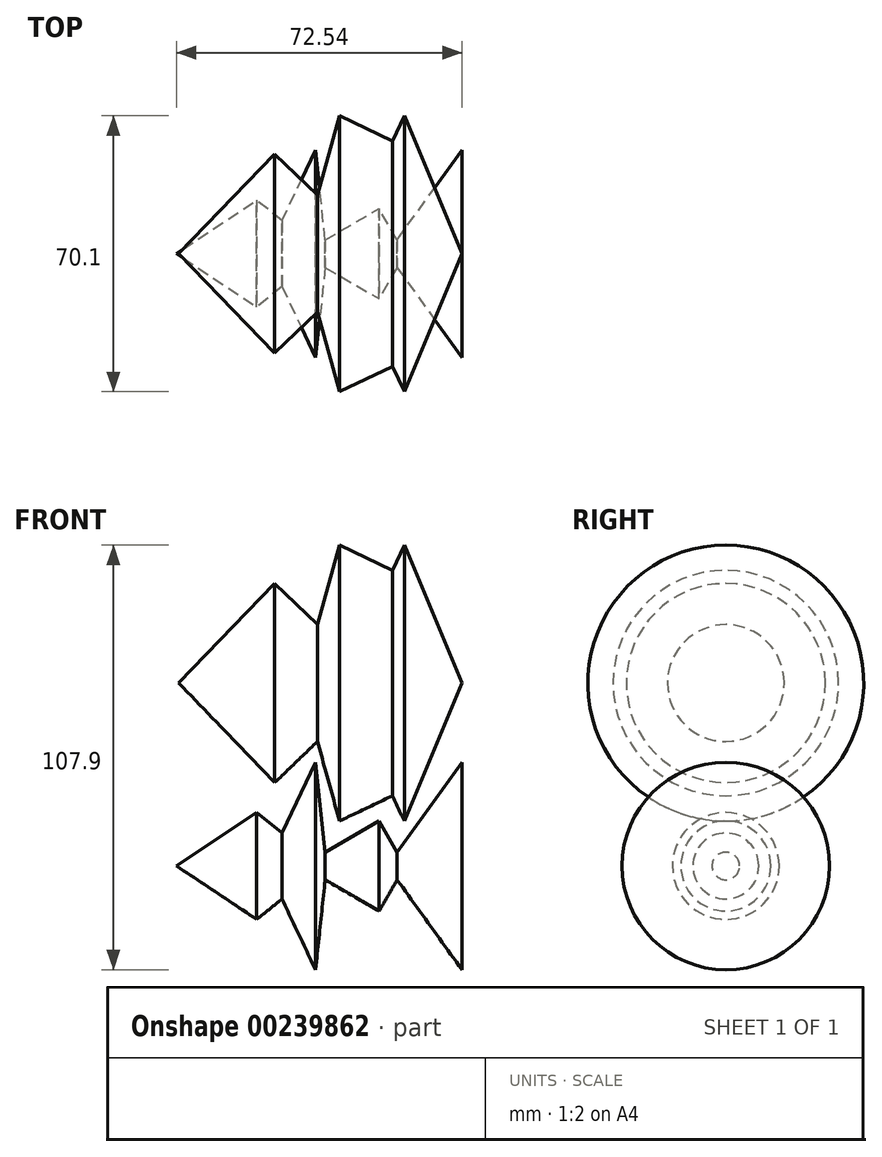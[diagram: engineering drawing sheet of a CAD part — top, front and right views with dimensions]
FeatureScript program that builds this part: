
annotation { "Feature Type Name" : "Feature", "Feature Type Description" : "" }
export const myFeature = defineFeature(function(context is Context, id is Id, definition is map)
    precondition{}
    {
        {
            var Q0;
            Q0=qCreatedBy(makeId("Front.planeOp"),FACE);
            var sketch = newSketch(context, id + "F0", { "sketchPlane" : qUnion([Q0])});
            skLineSegment(sketch, "E0", {"start": v(0, 0) * mm, "end": v(-72.54, 0) * mm});
            skLineSegment(sketch, "E1", {"start": v(-72.54, 0) * mm, "end": v(-52.12, 13.56) * mm});
            skLineSegment(sketch, "E2", {"start": v(-52.12, 13.56) * mm, "end": v(-45.72, 8.38) * mm});
            skLineSegment(sketch, "E3", {"start": v(-45.72, 8.38) * mm, "end": v(-37.19, 26.37) * mm});
            skLineSegment(sketch, "E4", {"start": v(-37.19, 26.37) * mm, "end": v(-34.75, 3.5) * mm});
            skLineSegment(sketch, "E5", {"start": v(-34.75, 3.5) * mm, "end": v(-21.03, 11.43) * mm});
            skLineSegment(sketch, "E6", {"start": v(-21.03, 11.43) * mm, "end": v(-16.45, 3.5) * mm});
            skLineSegment(sketch, "E7", {"start": v(-16.45, 3.5) * mm, "end": v(0, 26.37) * mm});
            skLineSegment(sketch, "E8", {"start": v(0, 26.37) * mm, "end": v(0, 0) * mm});
            skSolve(sketch);
        }
        {
            var Q0;
            Q0=qCreatedBy(makeId("Front.planeOp"),FACE);
            var sketch = newSketch(context, id + "F1", { "sketchPlane" : qUnion([Q0])});
            skLineSegment(sketch, "E9", {"start": v(0, 46.48) * mm, "end": v(-71.93, 46.48) * mm});
            skLineSegment(sketch, "E10", {"start": v(-71.93, 46.48) * mm, "end": v(-47.55, 21.18) * mm});
            skLineSegment(sketch, "E11", {"start": v(-47.55, 21.18) * mm, "end": v(-36.7, 31.64) * mm});
            skLineSegment(sketch, "E12", {"start": v(-36.7, 31.64) * mm, "end": v(-31.09, 11.43) * mm});
            skLineSegment(sketch, "E13", {"start": v(-31.09, 11.43) * mm, "end": v(-17.68, 17.83) * mm});
            skLineSegment(sketch, "E14", {"start": v(-17.68, 17.83) * mm, "end": v(-14.62, 11.43) * mm});
            skLineSegment(sketch, "E15", {"start": v(-14.62, 11.43) * mm, "end": v(0, 46.48) * mm});
            skSolve(sketch);
        }
        {
            var Q0;
            Q0=makeQuery(id+"F1.imprint","IMPRINT",FACE,{"disambiguationData":[TD([[makeQuery(id+"F1.imprint","IMPRINT",EDGE,{"derivedFrom":sQuery(id+"F1.wireOp",EDGE,"E9")}),1.0]])]});
            var Q1;
            Q1=sQuery(id+"F1.wireOp",EDGE,"E9");
            revolve(context, id + "F2", {"entities" : qUnion([Q0]), "axis" : qUnion([Q1]), "revolveType" : RevolveType.FULL});
        }
        {
            var Q0;
            Q0=makeQuery(id+"F0.imprint","IMPRINT",FACE,{"disambiguationData":[TD([[makeQuery(id+"F0.imprint","IMPRINT",EDGE,{"derivedFrom":sQuery(id+"F0.wireOp",EDGE,"E0")}),-1.0]])]});
            var Q1;
            Q1=sQuery(id+"F0.wireOp",EDGE,"E0");
            revolve(context, id + "F3", {"entities" : qUnion([Q0]), "axis" : qUnion([Q1]), "revolveType" : RevolveType.FULL});
        }
    });
